# Revit family: MADEL_GRILL_EXTERNAL_BLADE 50_DXT
name_source: partatom
category: Terminales de aire
revit_build: Autodesk Revit 2015 (Build: 20140606_1530(x64)
units: mm (PartAtom-declared; Revit-internal decimal feet)

## types (1)
- MADEL_GRILL_EXTERNAL_BLADE 50_DXT
    Afree = 0.1023 m²
    BIMETRICAL = http://www.bimetrical.com
    BIMETRICAL Category = AirTerminal
    Comentarios de tipo = The DXT series grilles are designed to take in air from the exterior or to expel used air. The fixed blades, 50 mm pitch, are designed to prevent rain penetration. They are very strongly built and resistant to aggressive climatic conditions, for outdoor installation.
    Descripción = MADEL_External grilles – blade 50
    Fabricante = MADEL
    Family Version = 1.0
    Flujo máx. = 1,657 m³/h
    Flujo mín. = 920 m³/h
    H = 300 mm
    H1 = 287 mm  [stored 0.941601 ft]
    H2 = 31.9 mm
    Height_Connector = 300 mm
    IfcExportAs = IfcAirTerminalType
    IfcExportType = IfcAirTerminalType
    Imagen de tipo = <Ninguno>
    L = 500 mm  [stored 1.64042 ft]
    Material Grill = MADEL_M9016
    Modelo = DXT+CX 500x300
    N_Graphic lines = 8
    Nº  Blades = 6
    Product Size = 500x300
    Review Date = 12/2016
    Revit Version = Revit 2015 - English
    URL = http://www.madel.com
    Vmax = 4.5 m/s
    Vmed = 3.5 m/s
    Vmin = 2.5 m/s
    Width_Connector = 500 mm  [stored 1.64042 ft]
    b_factor = 0.73101
    correction_factor = -9.935444
    m_factor = 1.80259

note: [stored X ft] marks values corroborated as IEEE doubles in the binary element streams (Revit-internal decimal feet)

## geometry (parser evidence)
native form markers: Blend x2
no freeform markers — native parametric forms only
